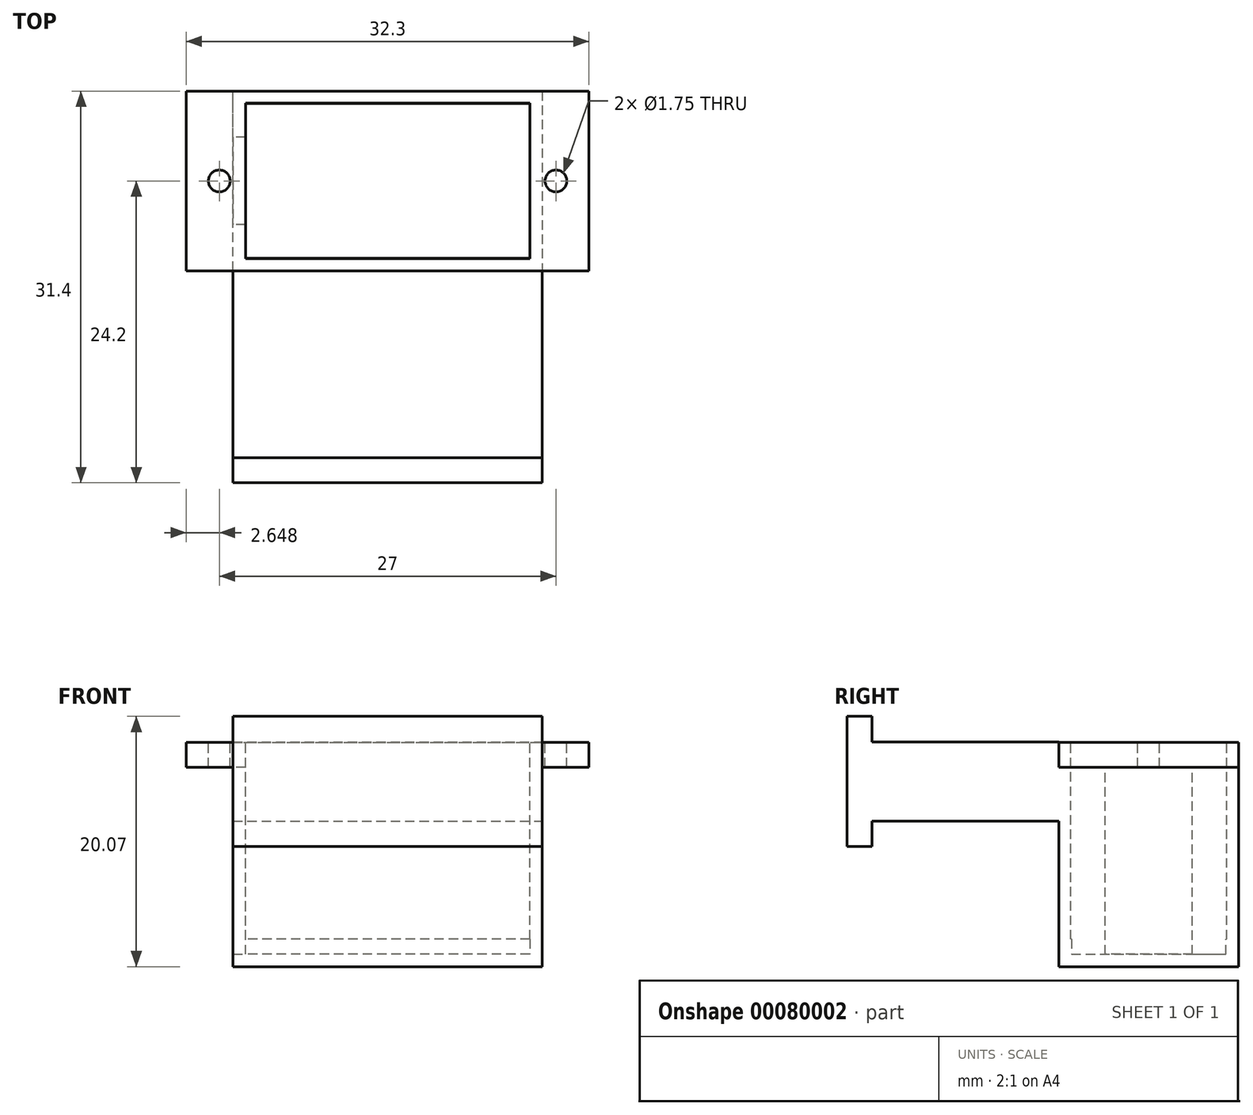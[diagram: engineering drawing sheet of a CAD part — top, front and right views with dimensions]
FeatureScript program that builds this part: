
annotation { "Feature Type Name" : "Feature", "Feature Type Description" : "" }
export const myFeature = defineFeature(function(context is Context, id is Id, definition is map)
    precondition{}
    {
        {
            var Q0;
            Q0=qCreatedBy(makeId("Front.planeOp"),FACE);
            var sketch = newSketch(context, id + "F0", { "sketchPlane" : qUnion([Q0])});
            skLineSegment(sketch, "E0", {"start": v(-29.12, 22.86) * mm, "end": v(-6.32, 22.86) * mm});
            skLineSegment(sketch, "E1", {"start": v(-6.32, 22.86) * mm, "end": v(-6.32, 6.86) * mm});
            skLineSegment(sketch, "E2", {"start": v(-6.32, 6.86) * mm, "end": v(-29.12, 6.86) * mm});
            skLineSegment(sketch, "E3", {"start": v(-29.12, 6.86) * mm, "end": v(-29.12, 22.86) * mm});
            skLineSegment(sketch, "E4.0", {"start": v(-30.12, 23.86) * mm, "end": v(-5.32, 23.86) * mm});
            skLineSegment(sketch, "E4.1", {"start": v(-30.12, 5.86) * mm, "end": v(-30.12, 23.86) * mm});
            skLineSegment(sketch, "E4.2", {"start": v(-5.32, 5.86) * mm, "end": v(-30.12, 5.86) * mm});
            skLineSegment(sketch, "E4.3", {"start": v(-5.32, 23.86) * mm, "end": v(-5.32, 5.86) * mm});
            skSolve(sketch);
        }
        {
            var Q0;
            Q0=makeQuery(id+"F0.imprint","IMPRINT",FACE,{"disambiguationData":[TD([[makeQuery(id+"F0.imprint","IMPRINT",EDGE,{"derivedFrom":sQuery(id+"F0.wireOp",EDGE,"E0")}),1.0]])]});
            extrude(context, id + "F1", {"entities" : qUnion([Q0]), "depth" : 6.2 * mm, "hasSecondDirection" : true, "secondDirectionOppositeDirection" : true, "secondDirectionDepth" : 6.2 * mm});
        }
        {
            var Q0;
            Q0=makeQuery(id+"F1.opExtrude","CAP_FACE",FACE,{"disambiguationData":[OSD([sQuery(id+"F0.wireOp",EDGE,"E0"),sQuery(id+"F0.wireOp",EDGE,"E1"),sQuery(id+"F0.wireOp",EDGE,"E2"),sQuery(id+"F0.wireOp",EDGE,"E3"),sQuery(id+"F0.wireOp",EDGE,"E4.0"),sQuery(id+"F0.wireOp",EDGE,"E4.1"),sQuery(id+"F0.wireOp",EDGE,"E4.2"),sQuery(id+"F0.wireOp",EDGE,"E4.3")])],"isStart":false});
            var sketch = newSketch(context, id + "F2", { "sketchPlane" : qUnion([Q0])});
            skLineSegment(sketch, "E5.bottom", {"start": v(-30.12, 23.86) * mm, "end": v(-5.32, 23.86) * mm});
            skLineSegment(sketch, "E5.top", {"start": v(-30.12, 5.86) * mm, "end": v(-5.32, 5.86) * mm});
            skLineSegment(sketch, "E5.left", {"start": v(-30.12, 23.86) * mm, "end": v(-30.12, 5.86) * mm});
            skLineSegment(sketch, "E5.right", {"start": v(-5.32, 23.86) * mm, "end": v(-5.32, 5.86) * mm});
            skSolve(sketch);
        }
        {
            var Q0;
            Q0 = qSketchRegion(id + "F2", true);
            extrude(context, id + "F3", {"entities" : qUnion([Q0]), "operationType" : NewBodyOperationType.ADD, "depth" : 1 * mm});
        }
        {
            var Q0;
            Q0=makeQuery(id+"F1.opExtrude","SWEPT_BODY",BODY,{"disambiguationData":[OSD([sQuery(id+"F0.wireOp",EDGE,"E0"),sQuery(id+"F0.wireOp",EDGE,"E1"),sQuery(id+"F0.wireOp",EDGE,"E2"),sQuery(id+"F0.wireOp",EDGE,"E3"),sQuery(id+"F0.wireOp",EDGE,"E4.0"),sQuery(id+"F0.wireOp",EDGE,"E4.1"),sQuery(id+"F0.wireOp",EDGE,"E4.2"),sQuery(id+"F0.wireOp",EDGE,"E4.3")])]});
            var Q1;
            Q1=qCreatedBy(makeId("Front.planeOp"),FACE);
            mirror(context, id + "F4", {"operationType" : NewBodyOperationType.ADD, "entities" : qUnion([Q0]), "mirrorPlane" : qUnion([Q1])});
        }
        {
            var Q0;
            {var subQ0=makeQuery(id+"F3.boolean.opBoolean","MERGE",FACE,{"derivedFrom":[makeQuery(id+"F1.opExtrude","SWEPT_FACE",FACE,{"disambiguationData":[OSD([sQuery(id+"F0.wireOp",EDGE,"E4.0")])]}),makeQuery(id+"F3.opExtrude","SWEPT_FACE",FACE,{"disambiguationData":[OSD([sQuery(id+"F2.wireOp",EDGE,"E5.bottom")])]})]});Q0=makeQuery(id+"F4.boolean.opBoolean","MERGE",FACE,{"derivedFrom":[subQ0,makeQuery(id+"F4.opPattern","COPY",FACE,{"derivedFrom":subQ0,"instanceName":"1"})]});}
            var sketch = newSketch(context, id + "F5", { "sketchPlane" : qUnion([Q0])});
            skLineSegment(sketch, "E6.bottom", {"start": v(-29.12, 6.24) * mm, "end": v(-6.32, 6.24) * mm});
            skLineSegment(sketch, "E6.top", {"start": v(-29.12, -6.24) * mm, "end": v(-6.32, -6.24) * mm});
            skLineSegment(sketch, "E6.left", {"start": v(-29.12, 6.24) * mm, "end": v(-29.12, -6.24) * mm});
            skLineSegment(sketch, "E6.right", {"start": v(-6.32, 6.24) * mm, "end": v(-6.32, -6.24) * mm});
            skPoint(sketch, "E7", {"position": v(-6.32, 0) * mm});
            skSolve(sketch);
        }
        {
            var Q0;
            Q0 = qSketchRegion(id + "F5", true);
            extrude(context, id + "F6", {"entities" : qUnion([Q0]), "operationType" : NewBodyOperationType.REMOVE, "oppositeDirection" : true, "depth" : 15.8 * mm});
        }
        {
            var Q0;
            {var subQ0=makeQuery(id+"F3.boolean.opBoolean","MERGE",FACE,{"derivedFrom":[makeQuery(id+"F1.opExtrude","SWEPT_FACE",FACE,{"disambiguationData":[OSD([sQuery(id+"F0.wireOp",EDGE,"E4.0")])]}),makeQuery(id+"F3.opExtrude","SWEPT_FACE",FACE,{"disambiguationData":[OSD([sQuery(id+"F2.wireOp",EDGE,"E5.bottom")])]})]});Q0=makeQuery(id+"F4.boolean.opBoolean","MERGE",FACE,{"derivedFrom":[subQ0,makeQuery(id+"F4.opPattern","COPY",FACE,{"derivedFrom":subQ0,"instanceName":"1"})]});}
            var sketch = newSketch(context, id + "F7", { "sketchPlane" : qUnion([Q0])});
            skLineSegment(sketch, "E8.bottom", {"start": v(-35.53, 3.5) * mm, "end": v(-26.53, 3.5) * mm});
            skLineSegment(sketch, "E8.top", {"start": v(-35.53, -3.5) * mm, "end": v(-26.53, -3.5) * mm});
            skLineSegment(sketch, "E8.left", {"start": v(-35.53, 3.5) * mm, "end": v(-35.53, -3.5) * mm});
            skLineSegment(sketch, "E8.right", {"start": v(-26.53, 3.5) * mm, "end": v(-26.53, -3.5) * mm});
            skPoint(sketch, "E9", {"position": v(-35.53, 0) * mm});
            skSolve(sketch);
        }
        {
            var Q0;
            Q0 = qSketchRegion(id + "F7", true);
            var Q1;
            Q1=makeQuery(id+"F1.opExtrude","SWEPT_FACE",FACE,{"disambiguationData":[OSD([sQuery(id+"F0.wireOp",EDGE,"E2")])]});
            extrude(context, id + "F8", {"entities" : qUnion([Q0]), "operationType" : NewBodyOperationType.REMOVE, "endBound" : BoundingType.UP_TO_SURFACE, "oppositeDirection" : true, "endBoundEntityFace" : qUnion([Q1]), "depth" : 25 * mm});
        }
        {
            var Q0;
            {var subQ0=makeQuery(id+"F3.boolean.opBoolean","MERGE",FACE,{"derivedFrom":[makeQuery(id+"F1.opExtrude","SWEPT_FACE",FACE,{"disambiguationData":[OSD([sQuery(id+"F0.wireOp",EDGE,"E4.0")])]}),makeQuery(id+"F3.opExtrude","SWEPT_FACE",FACE,{"disambiguationData":[OSD([sQuery(id+"F2.wireOp",EDGE,"E5.bottom")])]})]});Q0=makeQuery(id+"F4.boolean.opBoolean","MERGE",FACE,{"derivedFrom":[subQ0,makeQuery(id+"F4.opPattern","COPY",FACE,{"derivedFrom":subQ0,"instanceName":"1"})]});}
            var sketch = newSketch(context, id + "F9", { "sketchPlane" : qUnion([Q0])});
            skSolve(sketch);
        }
        {
            var Q0;
            {var subQ2=sQuery(id+"F2.wireOp",EDGE,"E5.bottom");var subQ3=makeQuery(id+"F3.opExtrude","CAP_EDGE",EDGE,{"disambiguationData":[OSD([subQ2])],"isStart":false});Q0=makeQuery(id+"F9.imprint","IMPRINT",FACE,{"disambiguationData":[TD([[makeQuery(id+"F9.imprint","IMPRINT",EDGE,{"derivedFrom":subQ3}),1.0]])]});}
            var sketch = newSketch(context, id + "F10", { "sketchPlane" : qUnion([Q0])});
            skLineSegment(sketch, "E10.bottom", {"start": v(-33.87, 7.2) * mm, "end": v(-1.57, 7.2) * mm});
            skLineSegment(sketch, "E10.top", {"start": v(-33.87, -7.2) * mm, "end": v(-1.57, -7.2) * mm});
            skLineSegment(sketch, "E10.left", {"start": v(-33.87, 7.2) * mm, "end": v(-33.87, -7.2) * mm});
            skLineSegment(sketch, "E10.right", {"start": v(-1.57, 7.2) * mm, "end": v(-1.57, -7.2) * mm});
            skPoint(sketch, "E11", {"position": v(-5.32, 0) * mm});
            skPoint(sketch, "E12", {"position": v(-1.57, 0) * mm});
            skPoint(sketch, "E13", {"position": v(-17.72, 7.2) * mm});
            skLineSegment(sketch, "E14.bottom", {"start": v(-29.12, 6.24) * mm, "end": v(-6.32, 6.24) * mm});
            skLineSegment(sketch, "E14.top", {"start": v(-29.12, -6.24) * mm, "end": v(-6.32, -6.24) * mm});
            skLineSegment(sketch, "E14.left", {"start": v(-29.12, 6.24) * mm, "end": v(-29.12, -6.24) * mm});
            skLineSegment(sketch, "E14.right", {"start": v(-6.32, 6.24) * mm, "end": v(-6.32, -6.24) * mm});
            skPoint(sketch, "E15", {"position": v(-17.72, 6.24) * mm});
            skSolve(sketch);
        }
        {
            var Q0;
            Q0 = qSketchRegion(id + "F10", true);
            extrude(context, id + "F11", {"entities" : qUnion([Q0]), "operationType" : NewBodyOperationType.ADD, "oppositeDirection" : true, "depth" : 2 * mm});
        }
        {
            var Q0;
            {var subQ0=makeQuery(id+"F3.boolean.opBoolean","MERGE",FACE,{"derivedFrom":[makeQuery(id+"F1.opExtrude","SWEPT_FACE",FACE,{"disambiguationData":[OSD([sQuery(id+"F0.wireOp",EDGE,"E4.0")])]}),makeQuery(id+"F3.opExtrude","SWEPT_FACE",FACE,{"disambiguationData":[OSD([sQuery(id+"F2.wireOp",EDGE,"E5.bottom")])]})]});Q0=makeQuery(id+"F11.boolean.opBoolean","MERGE",FACE,{"derivedFrom":[makeQuery(id+"F4.boolean.opBoolean","MERGE",FACE,{"derivedFrom":[subQ0,makeQuery(id+"F4.opPattern","COPY",FACE,{"derivedFrom":subQ0,"instanceName":"1"})]}),makeQuery(id+"F11.opExtrude","CAP_FACE",FACE,{"disambiguationData":[OSD([sQuery(id+"F10.wireOp",EDGE,"E10.bottom"),sQuery(id+"F10.wireOp",EDGE,"E10.top"),sQuery(id+"F10.wireOp",EDGE,"E10.left"),sQuery(id+"F10.wireOp",EDGE,"E10.right"),sQuery(id+"F10.wireOp",EDGE,"E14.bottom"),sQuery(id+"F10.wireOp",EDGE,"E14.top"),sQuery(id+"F10.wireOp",EDGE,"E14.left"),sQuery(id+"F10.wireOp",EDGE,"E14.right")])],"isStart":true})]});}
            var sketch = newSketch(context, id + "F12", { "sketchPlane" : qUnion([Q0])});
            skCircle(sketch, "E16", {"center": v(-31.22, 0) * mm, "radius": 0.88 * mm});
            skCircle(sketch, "E17", {"center": v(-4.22, 0) * mm, "radius": 0.88 * mm});
            skPoint(sketch, "E18", {"position": v(-17.72, -6.24) * mm});
            skSolve(sketch);
        }
        {
            var Q0;
            Q0 = qSketchRegion(id + "F12", true);
            extrude(context, id + "F13", {"entities" : qUnion([Q0]), "operationType" : NewBodyOperationType.REMOVE, "oppositeDirection" : true, "depth" : 25 * mm});
        }
        {
            var Q0;
            {var subQ0=makeQuery(id+"F3.boolean.opBoolean","MERGE",FACE,{"derivedFrom":[makeQuery(id+"F1.opExtrude","SWEPT_FACE",FACE,{"disambiguationData":[OSD([sQuery(id+"F0.wireOp",EDGE,"E4.3")])]}),makeQuery(id+"F3.opExtrude","SWEPT_FACE",FACE,{"disambiguationData":[OSD([sQuery(id+"F2.wireOp",EDGE,"E5.right")])]})]});Q0=makeQuery(id+"F4.boolean.opBoolean","MERGE",FACE,{"derivedFrom":[subQ0,makeQuery(id+"F4.opPattern","COPY",FACE,{"derivedFrom":subQ0,"instanceName":"1"})]});}
            var sketch = newSketch(context, id + "F14", { "sketchPlane" : qUnion([Q0])});
            skPoint(sketch, "E19", {"position": v(-24.67, 16.92) * mm});
            skPoint(sketch, "E20", {"position": v(-24.67, 13.74) * mm});
            skLineSegment(sketch, "E21", {"start": v(-7.2, 23.88) * mm, "end": v(-7.2, 17.54) * mm});
            skLineSegment(sketch, "E22", {"start": v(-22.2, 17.54) * mm, "end": v(-22.2, 15.48) * mm});
            skLineSegment(sketch, "E23", {"start": v(-22.2, 15.48) * mm, "end": v(-24.2, 15.48) * mm});
            skLineSegment(sketch, "E24", {"start": v(-24.2, 15.48) * mm, "end": v(-24.2, 25.93) * mm});
            skLineSegment(sketch, "E25", {"start": v(-24.2, 25.93) * mm, "end": v(-22.2, 25.93) * mm});
            skLineSegment(sketch, "E26", {"start": v(-22.2, 25.93) * mm, "end": v(-22.2, 23.88) * mm});
            skLineSegment(sketch, "E27", {"start": v(-22.2, 23.88) * mm, "end": v(-7.2, 23.88) * mm});
            skPoint(sketch, "E28", {"position": v(-24.2, 20.7) * mm});
            skPoint(sketch, "E29", {"position": v(-7.2, 20.7) * mm});
            skPoint(sketch, "E30.end.orphan", {"position": v(-19.44, 16.92) * mm});
            skPoint(sketch, "E31.end.orphan", {"position": v(-21.5, 14.92) * mm});
            skPoint(sketch, "E31.start.orphan", {"position": v(-21.5, 13.74) * mm});
            skPoint(sketch, "E32.end.orphan", {"position": v(-27.84, 13.74) * mm});
            skPoint(sketch, "E32.start.orphan", {"position": v(-27.84, 14.92) * mm});
            skPoint(sketch, "E33.end.orphan", {"position": v(-29.9, 14.92) * mm});
            skPoint(sketch, "E34.end.orphan", {"position": v(-29.9, 16.92) * mm});
            skLineSegment(sketch, "E35", {"start": v(-22.2, 17.54) * mm, "end": v(-7.2, 17.54) * mm});
            skSolve(sketch);
        }
        {
            var Q0;
            Q0=makeQuery(id+"F14.imprint","IMPRINT",FACE,{"disambiguationData":[TD([[makeQuery(id+"F14.imprint","IMPRINT",EDGE,{"derivedFrom":sQuery(id+"F14.wireOp",EDGE,"E21")}),-1.0]])]});
            var Q1;
            {var subQ0=makeQuery(id+"F3.boolean.opBoolean","MERGE",FACE,{"derivedFrom":[makeQuery(id+"F1.opExtrude","SWEPT_FACE",FACE,{"disambiguationData":[OSD([sQuery(id+"F0.wireOp",EDGE,"E4.1")])]}),makeQuery(id+"F3.opExtrude","SWEPT_FACE",FACE,{"disambiguationData":[OSD([sQuery(id+"F2.wireOp",EDGE,"E5.left")])]})]});Q1=makeQuery(id+"F4.boolean.opBoolean","MERGE",FACE,{"derivedFrom":[subQ0,makeQuery(id+"F4.opPattern","COPY",FACE,{"derivedFrom":subQ0,"instanceName":"1"})]});}
            extrude(context, id + "F15", {"entities" : qUnion([Q0]), "operationType" : NewBodyOperationType.ADD, "endBound" : BoundingType.UP_TO_SURFACE, "oppositeDirection" : true, "endBoundEntityFace" : qUnion([Q1]), "depth" : 25 * mm});
        }
    });
